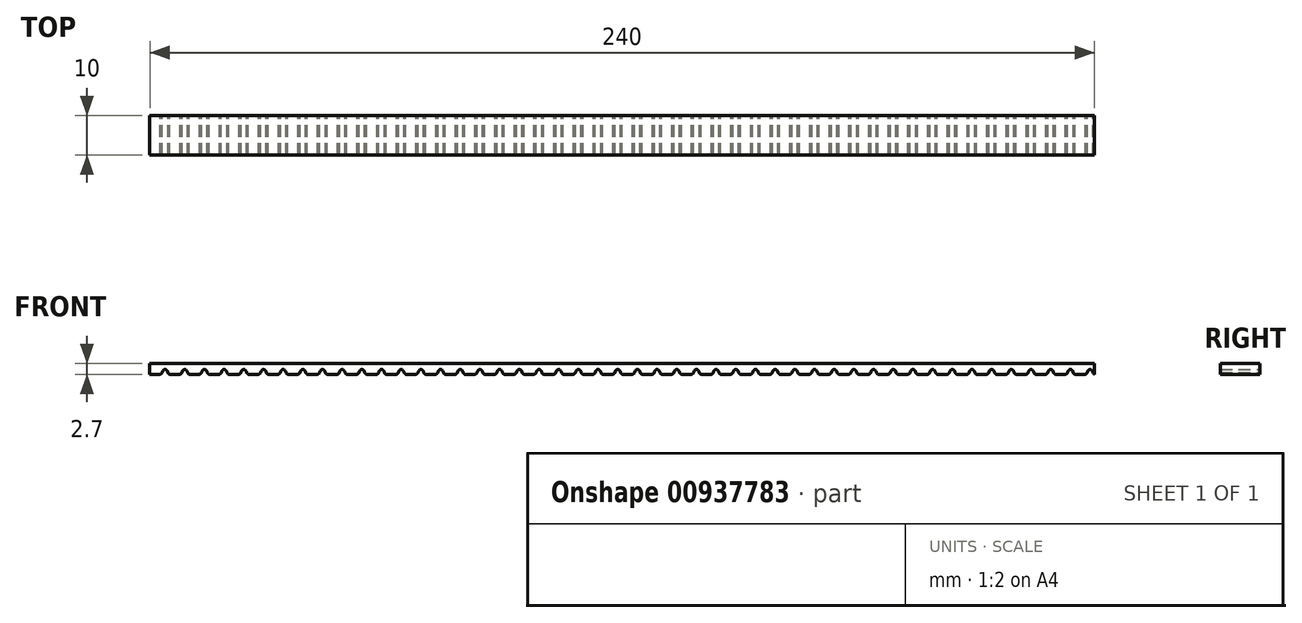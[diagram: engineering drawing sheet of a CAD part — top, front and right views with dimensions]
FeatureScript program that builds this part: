
annotation { "Feature Type Name" : "Feature", "Feature Type Description" : "" }
export const myFeature = defineFeature(function(context is Context, id is Id, definition is map)
    precondition{}
    {
        {
            var Q0;
            Q0=qCreatedBy(makeId("Front.planeOp"),FACE);
            var sketch = newSketch(context, id + "F0", { "sketchPlane" : qUnion([Q0])});
            skLineSegment(sketch, "E0", {"start": v(-120.76, -0.3) * mm, "end": v(-120.76, 0) * mm});
            skEllipticalArc(sketch, "E1.5.0.0", {});
            skArc(sketch, "E1.5.0.1", {"start": v(118.81, 0.14) * mm, "mid": v(118.98, -0.12) * mm, "end": v(119.24, -0.3) * mm});
            skArc(sketch, "E1.5.0.2", {"start": v(116.9, -0.3) * mm, "mid": v(117.2, -0.14) * mm, "end": v(117.39, 0.14) * mm});
            skEllipticalArc(sketch, "E1.5.0.3", {});
            skArc(sketch, "E2.1.0.0", {"start": v(113.81, 0.14) * mm, "mid": v(113.98, -0.12) * mm, "end": v(114.24, -0.3) * mm});
            skEllipticalArc(sketch, "E2.1.0.1", {});
            skEllipticalArc(sketch, "E2.1.0.2", {});
            skArc(sketch, "E2.1.0.3", {"start": v(111.9, -0.3) * mm, "mid": v(112.2, -0.14) * mm, "end": v(112.39, 0.14) * mm});
            skArc(sketch, "E2.2.0.0", {"start": v(108.81, 0.14) * mm, "mid": v(108.98, -0.12) * mm, "end": v(109.24, -0.3) * mm});
            skEllipticalArc(sketch, "E2.2.0.1", {});
            skEllipticalArc(sketch, "E2.2.0.2", {});
            skArc(sketch, "E2.2.0.3", {"start": v(106.9, -0.3) * mm, "mid": v(107.2, -0.14) * mm, "end": v(107.39, 0.14) * mm});
            skArc(sketch, "E2.3.0.0", {"start": v(103.81, 0.14) * mm, "mid": v(103.98, -0.12) * mm, "end": v(104.24, -0.3) * mm});
            skEllipticalArc(sketch, "E2.3.0.1", {});
            skEllipticalArc(sketch, "E2.3.0.2", {});
            skArc(sketch, "E2.3.0.3", {"start": v(101.9, -0.3) * mm, "mid": v(102.2, -0.14) * mm, "end": v(102.39, 0.14) * mm});
            skArc(sketch, "E2.4.0.0", {"start": v(98.81, 0.14) * mm, "mid": v(98.98, -0.12) * mm, "end": v(99.24, -0.3) * mm});
            skEllipticalArc(sketch, "E2.4.0.1", {});
            skEllipticalArc(sketch, "E2.4.0.2", {});
            skArc(sketch, "E2.4.0.3", {"start": v(96.9, -0.3) * mm, "mid": v(97.2, -0.14) * mm, "end": v(97.39, 0.14) * mm});
            skArc(sketch, "E2.5.0.0", {"start": v(93.81, 0.14) * mm, "mid": v(93.98, -0.12) * mm, "end": v(94.24, -0.3) * mm});
            skEllipticalArc(sketch, "E2.5.0.1", {});
            skEllipticalArc(sketch, "E2.5.0.2", {});
            skArc(sketch, "E2.5.0.3", {"start": v(91.9, -0.3) * mm, "mid": v(92.2, -0.14) * mm, "end": v(92.39, 0.14) * mm});
            skArc(sketch, "E2.6.0.0", {"start": v(88.81, 0.14) * mm, "mid": v(88.98, -0.12) * mm, "end": v(89.24, -0.3) * mm});
            skEllipticalArc(sketch, "E2.6.0.1", {});
            skEllipticalArc(sketch, "E2.6.0.2", {});
            skArc(sketch, "E2.6.0.3", {"start": v(86.9, -0.3) * mm, "mid": v(87.2, -0.14) * mm, "end": v(87.39, 0.14) * mm});
            skArc(sketch, "E2.7.0.0", {"start": v(83.81, 0.14) * mm, "mid": v(83.98, -0.12) * mm, "end": v(84.24, -0.3) * mm});
            skEllipticalArc(sketch, "E2.7.0.1", {});
            skEllipticalArc(sketch, "E2.7.0.2", {});
            skArc(sketch, "E2.7.0.3", {"start": v(81.9, -0.3) * mm, "mid": v(82.2, -0.14) * mm, "end": v(82.39, 0.14) * mm});
            skArc(sketch, "E2.8.0.0", {"start": v(78.81, 0.14) * mm, "mid": v(78.98, -0.12) * mm, "end": v(79.24, -0.3) * mm});
            skEllipticalArc(sketch, "E2.8.0.1", {});
            skEllipticalArc(sketch, "E2.8.0.2", {});
            skArc(sketch, "E2.8.0.3", {"start": v(76.9, -0.3) * mm, "mid": v(77.2, -0.14) * mm, "end": v(77.39, 0.14) * mm});
            skArc(sketch, "E2.9.0.0", {"start": v(73.81, 0.14) * mm, "mid": v(73.98, -0.12) * mm, "end": v(74.24, -0.3) * mm});
            skEllipticalArc(sketch, "E2.9.0.1", {});
            skEllipticalArc(sketch, "E2.9.0.2", {});
            skArc(sketch, "E2.9.0.3", {"start": v(71.9, -0.3) * mm, "mid": v(72.2, -0.14) * mm, "end": v(72.39, 0.14) * mm});
            skArc(sketch, "E2.10.0.0", {"start": v(68.81, 0.14) * mm, "mid": v(68.98, -0.12) * mm, "end": v(69.24, -0.3) * mm});
            skEllipticalArc(sketch, "E2.10.0.1", {});
            skEllipticalArc(sketch, "E2.10.0.2", {});
            skArc(sketch, "E2.10.0.3", {"start": v(66.9, -0.3) * mm, "mid": v(67.2, -0.14) * mm, "end": v(67.39, 0.14) * mm});
            skArc(sketch, "E2.11.0.0", {"start": v(63.81, 0.14) * mm, "mid": v(63.98, -0.12) * mm, "end": v(64.24, -0.3) * mm});
            skEllipticalArc(sketch, "E2.11.0.1", {});
            skEllipticalArc(sketch, "E2.11.0.2", {});
            skArc(sketch, "E2.11.0.3", {"start": v(61.9, -0.3) * mm, "mid": v(62.2, -0.14) * mm, "end": v(62.39, 0.14) * mm});
            skArc(sketch, "E2.12.0.0", {"start": v(58.81, 0.14) * mm, "mid": v(58.98, -0.12) * mm, "end": v(59.24, -0.3) * mm});
            skEllipticalArc(sketch, "E2.12.0.1", {});
            skEllipticalArc(sketch, "E2.12.0.2", {});
            skArc(sketch, "E2.12.0.3", {"start": v(56.9, -0.3) * mm, "mid": v(57.2, -0.14) * mm, "end": v(57.39, 0.14) * mm});
            skArc(sketch, "E2.13.0.0", {"start": v(53.81, 0.14) * mm, "mid": v(53.98, -0.12) * mm, "end": v(54.24, -0.3) * mm});
            skEllipticalArc(sketch, "E2.13.0.1", {});
            skEllipticalArc(sketch, "E2.13.0.2", {});
            skArc(sketch, "E2.13.0.3", {"start": v(51.9, -0.3) * mm, "mid": v(52.2, -0.14) * mm, "end": v(52.39, 0.14) * mm});
            skArc(sketch, "E2.14.0.0", {"start": v(48.81, 0.14) * mm, "mid": v(48.98, -0.12) * mm, "end": v(49.24, -0.3) * mm});
            skEllipticalArc(sketch, "E2.14.0.1", {});
            skEllipticalArc(sketch, "E2.14.0.2", {});
            skArc(sketch, "E2.14.0.3", {"start": v(46.9, -0.3) * mm, "mid": v(47.2, -0.14) * mm, "end": v(47.39, 0.14) * mm});
            skArc(sketch, "E2.15.0.0", {"start": v(43.81, 0.14) * mm, "mid": v(43.98, -0.12) * mm, "end": v(44.24, -0.3) * mm});
            skEllipticalArc(sketch, "E2.15.0.1", {});
            skEllipticalArc(sketch, "E2.15.0.2", {});
            skArc(sketch, "E2.15.0.3", {"start": v(41.9, -0.3) * mm, "mid": v(42.2, -0.14) * mm, "end": v(42.39, 0.14) * mm});
            skArc(sketch, "E2.16.0.0", {"start": v(38.81, 0.14) * mm, "mid": v(38.98, -0.12) * mm, "end": v(39.24, -0.3) * mm});
            skEllipticalArc(sketch, "E2.16.0.1", {});
            skEllipticalArc(sketch, "E2.16.0.2", {});
            skArc(sketch, "E2.16.0.3", {"start": v(36.9, -0.3) * mm, "mid": v(37.2, -0.14) * mm, "end": v(37.39, 0.14) * mm});
            skArc(sketch, "E2.17.0.0", {"start": v(33.81, 0.14) * mm, "mid": v(33.98, -0.12) * mm, "end": v(34.24, -0.3) * mm});
            skEllipticalArc(sketch, "E2.17.0.1", {});
            skEllipticalArc(sketch, "E2.17.0.2", {});
            skArc(sketch, "E2.17.0.3", {"start": v(31.9, -0.3) * mm, "mid": v(32.2, -0.14) * mm, "end": v(32.39, 0.14) * mm});
            skArc(sketch, "E2.18.0.0", {"start": v(28.81, 0.14) * mm, "mid": v(28.98, -0.12) * mm, "end": v(29.24, -0.3) * mm});
            skEllipticalArc(sketch, "E2.18.0.1", {});
            skEllipticalArc(sketch, "E2.18.0.2", {});
            skArc(sketch, "E2.18.0.3", {"start": v(26.9, -0.3) * mm, "mid": v(27.2, -0.14) * mm, "end": v(27.39, 0.14) * mm});
            skArc(sketch, "E2.19.0.0", {"start": v(23.81, 0.14) * mm, "mid": v(23.98, -0.12) * mm, "end": v(24.24, -0.3) * mm});
            skEllipticalArc(sketch, "E2.19.0.1", {});
            skEllipticalArc(sketch, "E2.19.0.2", {});
            skArc(sketch, "E2.19.0.3", {"start": v(21.9, -0.3) * mm, "mid": v(22.2, -0.14) * mm, "end": v(22.39, 0.14) * mm});
            skArc(sketch, "E2.20.0.0", {"start": v(18.81, 0.14) * mm, "mid": v(18.98, -0.12) * mm, "end": v(19.24, -0.3) * mm});
            skEllipticalArc(sketch, "E2.20.0.1", {});
            skEllipticalArc(sketch, "E2.20.0.2", {});
            skArc(sketch, "E2.20.0.3", {"start": v(16.9, -0.3) * mm, "mid": v(17.2, -0.14) * mm, "end": v(17.39, 0.14) * mm});
            skArc(sketch, "E2.21.0.0", {"start": v(13.81, 0.14) * mm, "mid": v(13.98, -0.12) * mm, "end": v(14.24, -0.3) * mm});
            skEllipticalArc(sketch, "E2.21.0.1", {});
            skEllipticalArc(sketch, "E2.21.0.2", {});
            skArc(sketch, "E2.21.0.3", {"start": v(11.9, -0.3) * mm, "mid": v(12.2, -0.14) * mm, "end": v(12.39, 0.14) * mm});
            skArc(sketch, "E2.22.0.0", {"start": v(8.81, 0.14) * mm, "mid": v(8.98, -0.12) * mm, "end": v(9.24, -0.3) * mm});
            skEllipticalArc(sketch, "E2.22.0.1", {});
            skEllipticalArc(sketch, "E2.22.0.2", {});
            skArc(sketch, "E2.22.0.3", {"start": v(6.9, -0.3) * mm, "mid": v(7.2, -0.14) * mm, "end": v(7.39, 0.14) * mm});
            skArc(sketch, "E2.23.0.0", {"start": v(3.81, 0.14) * mm, "mid": v(3.98, -0.12) * mm, "end": v(4.24, -0.3) * mm});
            skEllipticalArc(sketch, "E2.23.0.1", {});
            skEllipticalArc(sketch, "E2.23.0.2", {});
            skArc(sketch, "E2.23.0.3", {"start": v(1.9, -0.3) * mm, "mid": v(2.2, -0.14) * mm, "end": v(2.39, 0.14) * mm});
            skArc(sketch, "E2.24.0.0", {"start": v(-1.19, 0.14) * mm, "mid": v(-1.02, -0.12) * mm, "end": v(-0.76, -0.3) * mm});
            skEllipticalArc(sketch, "E2.24.0.1", {});
            skEllipticalArc(sketch, "E2.24.0.2", {});
            skArc(sketch, "E2.24.0.3", {"start": v(-3.1, -0.3) * mm, "mid": v(-2.8, -0.14) * mm, "end": v(-2.61, 0.14) * mm});
            skArc(sketch, "E2.25.0.0", {"start": v(-6.19, 0.14) * mm, "mid": v(-6.02, -0.12) * mm, "end": v(-5.76, -0.3) * mm});
            skEllipticalArc(sketch, "E2.25.0.1", {});
            skEllipticalArc(sketch, "E2.25.0.2", {});
            skArc(sketch, "E2.25.0.3", {"start": v(-8.1, -0.3) * mm, "mid": v(-7.8, -0.14) * mm, "end": v(-7.61, 0.14) * mm});
            skArc(sketch, "E2.26.0.0", {"start": v(-11.19, 0.14) * mm, "mid": v(-11.02, -0.12) * mm, "end": v(-10.76, -0.3) * mm});
            skEllipticalArc(sketch, "E2.26.0.1", {});
            skEllipticalArc(sketch, "E2.26.0.2", {});
            skArc(sketch, "E2.26.0.3", {"start": v(-13.1, -0.3) * mm, "mid": v(-12.8, -0.14) * mm, "end": v(-12.61, 0.14) * mm});
            skArc(sketch, "E2.27.0.0", {"start": v(-16.19, 0.14) * mm, "mid": v(-16.02, -0.12) * mm, "end": v(-15.76, -0.3) * mm});
            skEllipticalArc(sketch, "E2.27.0.1", {});
            skEllipticalArc(sketch, "E2.27.0.2", {});
            skArc(sketch, "E2.27.0.3", {"start": v(-18.1, -0.3) * mm, "mid": v(-17.8, -0.14) * mm, "end": v(-17.61, 0.14) * mm});
            skArc(sketch, "E2.28.0.0", {"start": v(-21.19, 0.14) * mm, "mid": v(-21.02, -0.12) * mm, "end": v(-20.76, -0.3) * mm});
            skEllipticalArc(sketch, "E2.28.0.1", {});
            skEllipticalArc(sketch, "E2.28.0.2", {});
            skArc(sketch, "E2.28.0.3", {"start": v(-23.1, -0.3) * mm, "mid": v(-22.8, -0.14) * mm, "end": v(-22.61, 0.14) * mm});
            skArc(sketch, "E2.29.0.0", {"start": v(-26.19, 0.14) * mm, "mid": v(-26.02, -0.12) * mm, "end": v(-25.76, -0.3) * mm});
            skEllipticalArc(sketch, "E2.29.0.1", {});
            skEllipticalArc(sketch, "E2.29.0.2", {});
            skArc(sketch, "E2.29.0.3", {"start": v(-28.1, -0.3) * mm, "mid": v(-27.8, -0.14) * mm, "end": v(-27.61, 0.14) * mm});
            skArc(sketch, "E2.30.0.0", {"start": v(-31.19, 0.14) * mm, "mid": v(-31.02, -0.12) * mm, "end": v(-30.76, -0.3) * mm});
            skEllipticalArc(sketch, "E2.30.0.1", {});
            skEllipticalArc(sketch, "E2.30.0.2", {});
            skArc(sketch, "E2.30.0.3", {"start": v(-33.1, -0.3) * mm, "mid": v(-32.8, -0.14) * mm, "end": v(-32.61, 0.14) * mm});
            skArc(sketch, "E2.31.0.0", {"start": v(-36.19, 0.14) * mm, "mid": v(-36.02, -0.12) * mm, "end": v(-35.76, -0.3) * mm});
            skEllipticalArc(sketch, "E2.31.0.1", {});
            skEllipticalArc(sketch, "E2.31.0.2", {});
            skArc(sketch, "E2.31.0.3", {"start": v(-38.1, -0.3) * mm, "mid": v(-37.8, -0.14) * mm, "end": v(-37.61, 0.14) * mm});
            skArc(sketch, "E2.32.0.0", {"start": v(-41.19, 0.14) * mm, "mid": v(-41.02, -0.12) * mm, "end": v(-40.76, -0.3) * mm});
            skEllipticalArc(sketch, "E2.32.0.1", {});
            skEllipticalArc(sketch, "E2.32.0.2", {});
            skArc(sketch, "E2.32.0.3", {"start": v(-43.1, -0.3) * mm, "mid": v(-42.8, -0.14) * mm, "end": v(-42.61, 0.14) * mm});
            skArc(sketch, "E2.33.0.0", {"start": v(-46.19, 0.14) * mm, "mid": v(-46.02, -0.12) * mm, "end": v(-45.76, -0.3) * mm});
            skEllipticalArc(sketch, "E2.33.0.1", {});
            skEllipticalArc(sketch, "E2.33.0.2", {});
            skArc(sketch, "E2.33.0.3", {"start": v(-48.1, -0.3) * mm, "mid": v(-47.8, -0.14) * mm, "end": v(-47.61, 0.14) * mm});
            skArc(sketch, "E2.34.0.0", {"start": v(-51.19, 0.14) * mm, "mid": v(-51.02, -0.12) * mm, "end": v(-50.76, -0.3) * mm});
            skEllipticalArc(sketch, "E2.34.0.1", {});
            skEllipticalArc(sketch, "E2.34.0.2", {});
            skArc(sketch, "E2.34.0.3", {"start": v(-53.1, -0.3) * mm, "mid": v(-52.8, -0.14) * mm, "end": v(-52.61, 0.14) * mm});
            skArc(sketch, "E2.35.0.0", {"start": v(-56.19, 0.14) * mm, "mid": v(-56.02, -0.12) * mm, "end": v(-55.76, -0.3) * mm});
            skEllipticalArc(sketch, "E2.35.0.1", {});
            skEllipticalArc(sketch, "E2.35.0.2", {});
            skArc(sketch, "E2.35.0.3", {"start": v(-58.1, -0.3) * mm, "mid": v(-57.8, -0.14) * mm, "end": v(-57.61, 0.14) * mm});
            skArc(sketch, "E2.36.0.0", {"start": v(-61.19, 0.14) * mm, "mid": v(-61.02, -0.12) * mm, "end": v(-60.76, -0.3) * mm});
            skEllipticalArc(sketch, "E2.36.0.1", {});
            skEllipticalArc(sketch, "E2.36.0.2", {});
            skArc(sketch, "E2.36.0.3", {"start": v(-63.1, -0.3) * mm, "mid": v(-62.8, -0.14) * mm, "end": v(-62.61, 0.14) * mm});
            skArc(sketch, "E2.37.0.0", {"start": v(-66.19, 0.14) * mm, "mid": v(-66.02, -0.12) * mm, "end": v(-65.76, -0.3) * mm});
            skEllipticalArc(sketch, "E2.37.0.1", {});
            skEllipticalArc(sketch, "E2.37.0.2", {});
            skArc(sketch, "E2.37.0.3", {"start": v(-68.1, -0.3) * mm, "mid": v(-67.8, -0.14) * mm, "end": v(-67.61, 0.14) * mm});
            skArc(sketch, "E2.38.0.0", {"start": v(-71.19, 0.14) * mm, "mid": v(-71.02, -0.12) * mm, "end": v(-70.76, -0.3) * mm});
            skEllipticalArc(sketch, "E2.38.0.1", {});
            skEllipticalArc(sketch, "E2.38.0.2", {});
            skArc(sketch, "E2.38.0.3", {"start": v(-73.1, -0.3) * mm, "mid": v(-72.8, -0.14) * mm, "end": v(-72.61, 0.14) * mm});
            skArc(sketch, "E2.39.0.0", {"start": v(-76.19, 0.14) * mm, "mid": v(-76.02, -0.12) * mm, "end": v(-75.76, -0.3) * mm});
            skEllipticalArc(sketch, "E2.39.0.1", {});
            skEllipticalArc(sketch, "E2.39.0.2", {});
            skArc(sketch, "E2.39.0.3", {"start": v(-78.1, -0.3) * mm, "mid": v(-77.8, -0.14) * mm, "end": v(-77.61, 0.14) * mm});
            skArc(sketch, "E2.40.0.0", {"start": v(-81.19, 0.14) * mm, "mid": v(-81.02, -0.12) * mm, "end": v(-80.76, -0.3) * mm});
            skEllipticalArc(sketch, "E2.40.0.1", {});
            skEllipticalArc(sketch, "E2.40.0.2", {});
            skArc(sketch, "E2.40.0.3", {"start": v(-83.1, -0.3) * mm, "mid": v(-82.8, -0.14) * mm, "end": v(-82.61, 0.14) * mm});
            skArc(sketch, "E2.41.0.0", {"start": v(-86.19, 0.14) * mm, "mid": v(-86.02, -0.12) * mm, "end": v(-85.76, -0.3) * mm});
            skEllipticalArc(sketch, "E2.41.0.1", {});
            skEllipticalArc(sketch, "E2.41.0.2", {});
            skArc(sketch, "E2.41.0.3", {"start": v(-88.1, -0.3) * mm, "mid": v(-87.8, -0.14) * mm, "end": v(-87.61, 0.14) * mm});
            skArc(sketch, "E2.42.0.0", {"start": v(-91.19, 0.14) * mm, "mid": v(-91.02, -0.12) * mm, "end": v(-90.76, -0.3) * mm});
            skEllipticalArc(sketch, "E2.42.0.1", {});
            skEllipticalArc(sketch, "E2.42.0.2", {});
            skArc(sketch, "E2.42.0.3", {"start": v(-93.1, -0.3) * mm, "mid": v(-92.8, -0.14) * mm, "end": v(-92.61, 0.14) * mm});
            skArc(sketch, "E2.43.0.0", {"start": v(-96.19, 0.14) * mm, "mid": v(-96.02, -0.12) * mm, "end": v(-95.76, -0.3) * mm});
            skEllipticalArc(sketch, "E2.43.0.1", {});
            skEllipticalArc(sketch, "E2.43.0.2", {});
            skArc(sketch, "E2.43.0.3", {"start": v(-98.1, -0.3) * mm, "mid": v(-97.8, -0.14) * mm, "end": v(-97.61, 0.14) * mm});
            skArc(sketch, "E2.44.0.0", {"start": v(-101.19, 0.14) * mm, "mid": v(-101.02, -0.12) * mm, "end": v(-100.76, -0.3) * mm});
            skEllipticalArc(sketch, "E2.44.0.1", {});
            skEllipticalArc(sketch, "E2.44.0.2", {});
            skArc(sketch, "E2.44.0.3", {"start": v(-103.1, -0.3) * mm, "mid": v(-102.8, -0.14) * mm, "end": v(-102.61, 0.14) * mm});
            skArc(sketch, "E2.45.0.0", {"start": v(-106.19, 0.14) * mm, "mid": v(-106.02, -0.12) * mm, "end": v(-105.76, -0.3) * mm});
            skEllipticalArc(sketch, "E2.45.0.1", {});
            skEllipticalArc(sketch, "E2.45.0.2", {});
            skArc(sketch, "E2.45.0.3", {"start": v(-108.1, -0.3) * mm, "mid": v(-107.8, -0.14) * mm, "end": v(-107.61, 0.14) * mm});
            skArc(sketch, "E2.46.0.0", {"start": v(-111.19, 0.14) * mm, "mid": v(-111.02, -0.12) * mm, "end": v(-110.76, -0.3) * mm});
            skEllipticalArc(sketch, "E2.46.0.1", {});
            skEllipticalArc(sketch, "E2.46.0.2", {});
            skArc(sketch, "E2.46.0.3", {"start": v(-113.1, -0.3) * mm, "mid": v(-112.8, -0.14) * mm, "end": v(-112.61, 0.14) * mm});
            skArc(sketch, "E2.47.0.0", {"start": v(-116.19, 0.14) * mm, "mid": v(-116.02, -0.12) * mm, "end": v(-115.76, -0.3) * mm});
            skEllipticalArc(sketch, "E2.47.0.1", {});
            skEllipticalArc(sketch, "E2.47.0.2", {});
            skArc(sketch, "E2.47.0.3", {"start": v(-118.1, -0.3) * mm, "mid": v(-117.8, -0.14) * mm, "end": v(-117.61, 0.14) * mm});
            skLineSegment(sketch, "E2.direction1", {"start": v(116.9, -0.3) * mm, "end": v(114.24, -0.3) * mm, "construction": true});
            skLineSegment(sketch, "E3.trimOffspring", {"start": v(-118.1, -0.3) * mm, "end": v(-120.76, -0.3) * mm});
            skLineSegment(sketch, "E4.trimOffspring", {"start": v(-113.1, -0.3) * mm, "end": v(-115.76, -0.3) * mm});
            skLineSegment(sketch, "E5", {"start": v(119.24, 0) * mm, "end": v(119.24, -0.3) * mm});
            skPoint(sketch, "E6.orphan", {"position": v(119.24, 0) * mm});
            skLineSegment(sketch, "E7.trimOffspring", {"start": v(111.9, -0.3) * mm, "end": v(109.24, -0.3) * mm});
            skLineSegment(sketch, "E8.trimOffspring", {"start": v(101.9, -0.3) * mm, "end": v(99.24, -0.3) * mm});
            skLineSegment(sketch, "E9.trimOffspring", {"start": v(106.9, -0.3) * mm, "end": v(104.24, -0.3) * mm});
            skLineSegment(sketch, "E10", {"start": v(116.9, -0.3) * mm, "end": v(114.24, -0.3) * mm});
            skLineSegment(sketch, "E11.trimOffspring", {"start": v(96.9, -0.3) * mm, "end": v(94.24, -0.3) * mm});
            skLineSegment(sketch, "E12.trimOffspring", {"start": v(91.9, -0.3) * mm, "end": v(89.24, -0.3) * mm});
            skLineSegment(sketch, "E13.trimOffspring", {"start": v(86.9, -0.3) * mm, "end": v(84.24, -0.3) * mm});
            skLineSegment(sketch, "E14.trimOffspring", {"start": v(81.9, -0.3) * mm, "end": v(79.24, -0.3) * mm});
            skLineSegment(sketch, "E15.trimOffspring", {"start": v(76.9, -0.3) * mm, "end": v(74.24, -0.3) * mm});
            skLineSegment(sketch, "E16.trimOffspring", {"start": v(71.9, -0.3) * mm, "end": v(69.24, -0.3) * mm});
            skLineSegment(sketch, "E17.trimOffspring", {"start": v(66.9, -0.3) * mm, "end": v(64.24, -0.3) * mm});
            skLineSegment(sketch, "E18.trimOffspring", {"start": v(61.9, -0.3) * mm, "end": v(59.24, -0.3) * mm});
            skLineSegment(sketch, "E19.trimOffspring", {"start": v(56.9, -0.3) * mm, "end": v(54.24, -0.3) * mm});
            skLineSegment(sketch, "E20.trimOffspring", {"start": v(51.9, -0.3) * mm, "end": v(49.24, -0.3) * mm});
            skLineSegment(sketch, "E21.trimOffspring", {"start": v(46.9, -0.3) * mm, "end": v(44.24, -0.3) * mm});
            skLineSegment(sketch, "E22.trimOffspring", {"start": v(41.9, -0.3) * mm, "end": v(39.24, -0.3) * mm});
            skLineSegment(sketch, "E23.trimOffspring", {"start": v(36.9, -0.3) * mm, "end": v(34.24, -0.3) * mm});
            skLineSegment(sketch, "E24.trimOffspring", {"start": v(31.9, -0.3) * mm, "end": v(29.24, -0.3) * mm});
            skLineSegment(sketch, "E25.trimOffspring", {"start": v(26.9, -0.3) * mm, "end": v(24.24, -0.3) * mm});
            skLineSegment(sketch, "E26.trimOffspring", {"start": v(21.9, -0.3) * mm, "end": v(19.24, -0.3) * mm});
            skLineSegment(sketch, "E27.trimOffspring", {"start": v(16.9, -0.3) * mm, "end": v(14.24, -0.3) * mm});
            skLineSegment(sketch, "E28.trimOffspring", {"start": v(11.9, -0.3) * mm, "end": v(9.24, -0.3) * mm});
            skLineSegment(sketch, "E29.trimOffspring", {"start": v(6.9, -0.3) * mm, "end": v(4.24, -0.3) * mm});
            skLineSegment(sketch, "E30.trimOffspring", {"start": v(1.9, -0.3) * mm, "end": v(-0.76, -0.3) * mm});
            skLineSegment(sketch, "E31.trimOffspring", {"start": v(-3.1, -0.3) * mm, "end": v(-5.76, -0.3) * mm});
            skLineSegment(sketch, "E32.trimOffspring", {"start": v(-8.1, -0.3) * mm, "end": v(-10.76, -0.3) * mm});
            skLineSegment(sketch, "E33.trimOffspring", {"start": v(-13.1, -0.3) * mm, "end": v(-15.76, -0.3) * mm});
            skLineSegment(sketch, "E34.trimOffspring", {"start": v(-18.1, -0.3) * mm, "end": v(-20.76, -0.3) * mm});
            skLineSegment(sketch, "E35.trimOffspring", {"start": v(-23.1, -0.3) * mm, "end": v(-25.76, -0.3) * mm});
            skLineSegment(sketch, "E36.trimOffspring", {"start": v(-28.1, -0.3) * mm, "end": v(-30.76, -0.3) * mm});
            skLineSegment(sketch, "E37.trimOffspring", {"start": v(-33.1, -0.3) * mm, "end": v(-35.76, -0.3) * mm});
            skLineSegment(sketch, "E38.trimOffspring", {"start": v(-38.1, -0.3) * mm, "end": v(-40.76, -0.3) * mm});
            skLineSegment(sketch, "E39.trimOffspring", {"start": v(-43.1, -0.3) * mm, "end": v(-45.76, -0.3) * mm});
            skLineSegment(sketch, "E40.trimOffspring", {"start": v(-48.1, -0.3) * mm, "end": v(-50.76, -0.3) * mm});
            skLineSegment(sketch, "E41.trimOffspring", {"start": v(-53.1, -0.3) * mm, "end": v(-55.76, -0.3) * mm});
            skLineSegment(sketch, "E42.trimOffspring", {"start": v(-58.1, -0.3) * mm, "end": v(-60.76, -0.3) * mm});
            skLineSegment(sketch, "E43.trimOffspring", {"start": v(-63.1, -0.3) * mm, "end": v(-65.76, -0.3) * mm});
            skLineSegment(sketch, "E44.trimOffspring", {"start": v(-68.1, -0.3) * mm, "end": v(-70.76, -0.3) * mm});
            skLineSegment(sketch, "E45.trimOffspring", {"start": v(-73.1, -0.3) * mm, "end": v(-75.76, -0.3) * mm});
            skLineSegment(sketch, "E46.trimOffspring", {"start": v(-78.1, -0.3) * mm, "end": v(-80.76, -0.3) * mm});
            skLineSegment(sketch, "E47.trimOffspring", {"start": v(-83.1, -0.3) * mm, "end": v(-85.76, -0.3) * mm});
            skLineSegment(sketch, "E48.trimOffspring", {"start": v(-88.1, -0.3) * mm, "end": v(-90.76, -0.3) * mm});
            skLineSegment(sketch, "E49.trimOffspring", {"start": v(-93.1, -0.3) * mm, "end": v(-95.76, -0.3) * mm});
            skLineSegment(sketch, "E50.trimOffspring", {"start": v(-98.1, -0.3) * mm, "end": v(-100.76, -0.3) * mm});
            skLineSegment(sketch, "E51.trimOffspring", {"start": v(-103.1, -0.3) * mm, "end": v(-105.76, -0.3) * mm});
            skLineSegment(sketch, "E52.trimOffspring", {"start": v(-108.1, -0.3) * mm, "end": v(-110.76, -0.3) * mm});
            skPoint(sketch, "E53.orphan", {"position": v(119.24, 2.4) * mm});
            skLineSegment(sketch, "E54", {"start": v(119.24, -0.3) * mm, "end": v(119.24, 2.4) * mm});
            skLineSegment(sketch, "E55", {"start": v(-120.76, -0.3) * mm, "end": v(-120.76, 2.4) * mm});
            skLineSegment(sketch, "E56", {"start": v(-120.76, 2.4) * mm, "end": v(119.24, 2.4) * mm});
            const initialGuessF0  = {"E1.5.0.0": [0.11808504036189091, -0.0001, 0, 1, 0.001, 0.0007199110732306023, 0, 1.3242255138486458], "E1.5.0.3": [0.11808504036189114, -0.0001, 0, 1, 0.001, 0.00075, 4.958959793090693, 0], "E2.1.0.1": [0.11308504036189114, -0.0001, 0, 1, 0.001, 0.00075, 4.958959793090693, 0], "E2.1.0.2": [0.1130850403618909, -0.0001, 0, 1, 0.001, 0.0007199110732306023, 0, 1.3242255138486458], "E2.2.0.1": [0.10808504036189115, -0.0001, 0, 1, 0.001, 0.00075, 4.958959793090693, 0], "E2.2.0.2": [0.10808504036189091, -0.0001, 0, 1, 0.001, 0.0007199110732306023, 0, 1.3242255138486458], "E2.3.0.1": [0.10308504036189114, -0.0001, 0, 1, 0.001, 0.00075, 4.958959793090693, 0], "E2.3.0.2": [0.10308504036189091, -0.0001, 0, 1, 0.001, 0.0007199110732306023, 0, 1.3242255138486458], "E2.4.0.1": [0.09808504036189114, -0.0001, 0, 1, 0.001, 0.00075, 4.958959793090693, 0], "E2.4.0.2": [0.0980850403618909, -0.0001, 0, 1, 0.001, 0.0007199110732306023, 0, 1.3242255138486458], "E2.5.0.1": [0.09308504036189114, -0.0001, 0, 1, 0.001, 0.00075, 4.95895979309069, 0], "E2.5.0.2": [0.09308504036189091, -0.0001, 0, 1, 0.001, 0.0007199110732306023, 0, 1.3242255138486458], "E2.6.0.1": [0.08808504036189115, -0.0001, 0, 1, 0.001, 0.00075, 4.958959793090693, 0], "E2.6.0.2": [0.08808504036189091, -0.0001, 0, 1, 0.001, 0.0007199110732306023, 0, 1.3242255138486458], "E2.7.0.1": [0.08308504036189114, -0.0001, 0, 1, 0.001, 0.00075, 4.958959793090693, 0], "E2.7.0.2": [0.0830850403618909, -0.0001, 0, 1, 0.001, 0.0007199110732306023, 0, 1.3242255138486458], "E2.8.0.1": [0.07808504036189115, -0.0001, 0, 1, 0.001, 0.00075, 4.9589597930906955, 0], "E2.8.0.2": [0.0780850403618909, -0.0001, 0, 1, 0.001, 0.0007199110732306023, 0, 1.3242255138486458], "E2.9.0.1": [0.07308504036189115, -0.0001, 0, 1, 0.001, 0.00075, 4.958959793090693, 0], "E2.9.0.2": [0.07308504036189091, -0.0001, 0, 1, 0.001, 0.0007199110732306023, 0, 1.3242255138486458], "E2.10.0.1": [0.06808504036189114, -0.0001, 0, 1, 0.001, 0.00075, 4.958959793090693, 0], "E2.10.0.2": [0.0680850403618909, -0.0001, 0, 1, 0.001, 0.0007199110732306023, 0, 1.3242255138486458], "E2.11.0.1": [0.06308504036189114, -0.0001, 0, 1, 0.001, 0.00075, 4.95895979309069, 0], "E2.11.0.2": [0.06308504036189092, -0.0001, 0, 1, 0.001, 0.0007199110732306023, 0, 1.324225513848647], "E2.12.0.1": [0.058085040361891146, -0.0001, 0, 1, 0.001, 0.00075, 4.958959793090693, 6.283185307179582], "E2.12.0.2": [0.05808504036189091, -0.0001, 0, 1, 0.001, 0.0007199110732306023, 0, 1.3242255138486458], "E2.13.0.1": [0.05308504036189114, -0.0001, 0, 1, 0.001, 0.00075, 4.958959793090693, 6.283185307179582], "E2.13.0.2": [0.053085040361890906, -0.0001, 0, 1, 0.001, 0.0007199110732306023, 0, 1.3242255138486458], "E2.14.0.1": [0.04808504036189114, -0.0001, 0, 1, 0.001, 0.00075, 4.958959793090693, 6.283185307179582], "E2.14.0.2": [0.0480850403618909, -0.0001, 0, 1, 0.001, 0.0007199110732306023, 0, 1.3242255138486458], "E2.15.0.1": [0.04308504036189115, -0.0001, 0, 1, 0.001, 0.00075, 4.958959793090693, 6.283185307179582], "E2.15.0.2": [0.04308504036189091, -0.0001, 0, 1, 0.001, 0.0007199110732306023, 0, 1.3242255138486458], "E2.16.0.1": [0.03808504036189114, -0.0001, 0, 1, 0.001, 0.00075, 4.958959793090693, 6.283185307179582], "E2.16.0.2": [0.03808504036189091, -0.0001, 0, 1, 0.001, 0.0007199110732306023, 0, 1.3242255138486458], "E2.17.0.1": [0.03308504036189114, -0.0001, 0, 1, 0.001, 0.00075, 4.958959793090693, 6.283185307179582], "E2.17.0.2": [0.0330850403618909, -0.0001, 0, 1, 0.001, 0.0007199110732306023, 0, 1.3242255138486458], "E2.18.0.1": [0.028085040361891148, -0.0001, 0, 1, 0.001, 0.00075, 4.958959793090693, 0], "E2.18.0.2": [0.02808504036189091, -0.0001, 0, 1, 0.001, 0.0007199110732306023, 0, 1.3242255138486458], "E2.19.0.1": [0.023085040361891143, -0.0001, 0, 1, 0.001, 0.00075, 4.958959793090693, 0], "E2.19.0.2": [0.023085040361890907, -0.0001, 0, 1, 0.001, 0.0007199110732306023, 0, 1.3242255138486458], "E2.20.0.1": [0.01808504036189114, -0.0001, 0, 1, 0.001, 0.00075, 4.958959793090693, 0], "E2.20.0.2": [0.018085040361890903, -0.0001, 0, 1, 0.001, 0.0007199110732306023, 0, 1.3242255138486458], "E2.21.0.1": [0.013085040361891148, -0.0001, 0, 1, 0.001, 0.00075, 4.958959793090693, 0], "E2.21.0.2": [0.013085040361890912, -0.0001, 0, 1, 0.001, 0.0007199110732306023, 0, 1.3242255138486458], "E2.22.0.1": [0.008085040361891144, -0.0001, 0, 1, 0.001, 0.00075, 4.958959793090693, 0], "E2.22.0.2": [0.008085040361890908, -0.0001, 0, 1, 0.001, 0.0007199110732306023, 0, 1.3242255138486458], "E2.23.0.1": [0.0030850403618911393, -0.0001, 0, 1, 0.001, 0.00075, 4.958959793090693, 0], "E2.23.0.2": [0.0030850403618909034, -0.0001, 0, 1, 0.001, 0.0007199110732306023, 0, 1.3242255138486458], "E2.24.0.1": [-0.0019149596381088513, -0.0001, 0, 1, 0.001, 0.00075, 4.958959793090693, 0], "E2.24.0.2": [-0.0019149596381090872, -0.0001, 0, 1, 0.001, 0.0007199110732306023, 0, 1.3242255138486458], "E2.25.0.1": [-0.006914959638108856, -0.0001, 0, 1, 0.001, 0.00075, 4.958959793090693, 0], "E2.25.0.2": [-0.006914959638109092, -0.0001, 0, 1, 0.001, 0.0007199110732306023, 0, 1.3242255138486458], "E2.26.0.1": [-0.01191495963810886, -0.0001, 0, 1, 0.001, 0.00075, 4.958959793090693, 0], "E2.26.0.2": [-0.011914959638109096, -0.0001, 0, 1, 0.001, 0.0007199110732306023, 0, 1.3242255138486458], "E2.27.0.1": [-0.016914959638108865, -0.0001, 0, 1, 0.001, 0.00075, 4.958959793090693, 0], "E2.27.0.2": [-0.0169149596381091, -0.0001, 0, 1, 0.001, 0.0007199110732306023, 0, 1.3242255138486458], "E2.28.0.1": [-0.02191495963810887, -0.0001, 0, 1, 0.001, 0.00075, 4.958959793090693, 0], "E2.28.0.2": [-0.021914959638109105, -0.0001, 0, 1, 0.001, 0.0007199110732306023, 0, 1.3242255138486458], "E2.29.0.1": [-0.026914959638108846, -0.0001, 0, 1, 0.001, 0.00075, 4.958959793090693, 0], "E2.29.0.2": [-0.02691495963810908, -0.0001, 0, 1, 0.001, 0.0007199110732306023, 0, 1.3242255138486458], "E2.30.0.1": [-0.03191495963810885, -0.0001, 0, 1, 0.001, 0.00075, 4.958959793090693, 6.283185307179582], "E2.30.0.2": [-0.031914959638109086, -0.0001, 0, 1, 0.001, 0.0007199110732306023, 0, 1.3242255138486458], "E2.31.0.1": [-0.036914959638108855, -0.0001, 0, 1, 0.001, 0.00075, 4.958959793090693, 6.283185307179582], "E2.31.0.2": [-0.03691495963810909, -0.0001, 0, 1, 0.001, 0.0007199110732306023, 0, 1.3242255138486458], "E2.32.0.1": [-0.04191495963810886, -0.0001, 0, 1, 0.001, 0.00075, 4.958959793090693, 6.283185307179582], "E2.32.0.2": [-0.041914959638109095, -0.0001, 0, 1, 0.001, 0.0007199110732306023, 0, 1.3242255138486458], "E2.33.0.1": [-0.046914959638108863, -0.0001, 0, 1, 0.001, 0.00075, 4.958959793090693, 6.283185307179582], "E2.33.0.2": [-0.0469149596381091, -0.0001, 0, 1, 0.001, 0.0007199110732306023, 0, 1.3242255138486458], "E2.34.0.1": [-0.05191495963810887, -0.0001, 0, 1, 0.001, 0.00075, 4.958959793090693, 6.283185307179582], "E2.34.0.2": [-0.051914959638109104, -0.0001, 0, 1, 0.001, 0.0007199110732306023, 0, 1.3242255138486458], "E2.35.0.1": [-0.05691495963810887, -0.0001, 0, 1, 0.001, 0.00075, 4.958959793090693, 6.283185307179582], "E2.35.0.2": [-0.05691495963810911, -0.0001, 0, 1, 0.001, 0.0007199110732306023, 0, 1.3242255138486458], "E2.36.0.1": [-0.06191495963810885, -0.0001, 0, 1, 0.001, 0.00075, 4.958959793090693, 6.283185307179582], "E2.36.0.2": [-0.061914959638109085, -0.0001, 0, 1, 0.001, 0.0007199110732306023, 0, 1.3242255138486458], "E2.37.0.1": [-0.06691495963810885, -0.0001, 0, 1, 0.001, 0.00075, 4.958959793090693, 0], "E2.37.0.2": [-0.06691495963810909, -0.0001, 0, 1, 0.001, 0.0007199110732306023, 0, 1.3242255138486458], "E2.38.0.1": [-0.07191495963810886, -0.0001, 0, 1, 0.001, 0.00075, 4.958959793090693, 0], "E2.38.0.2": [-0.0719149596381091, -0.0001, 0, 1, 0.001, 0.0007199110732306023, 0, 1.3242255138486458], "E2.39.0.1": [-0.07691495963810886, -0.0001, 0, 1, 0.001, 0.00075, 4.958959793090693, 0], "E2.39.0.2": [-0.0769149596381091, -0.0001, 0, 1, 0.001, 0.0007199110732306023, 0, 1.3242255138486458], "E2.40.0.1": [-0.08191495963810887, -0.0001, 0, 1, 0.001, 0.00075, 4.958959793090693, 0], "E2.40.0.2": [-0.0819149596381091, -0.0001, 0, 1, 0.001, 0.0007199110732306023, 0, 1.3242255138486458], "E2.41.0.1": [-0.08691495963810887, -0.0001, 0, 1, 0.001, 0.00075, 4.958959793090693, 0], "E2.41.0.2": [-0.08691495963810911, -0.0001, 0, 1, 0.001, 0.0007199110732306023, 0, 1.3242255138486458], "E2.42.0.1": [-0.09191495963810885, -0.0001, 0, 1, 0.001, 0.00075, 4.958959793090693, 0], "E2.42.0.2": [-0.09191495963810908, -0.0001, 0, 1, 0.001, 0.0007199110732306023, 0, 1.3242255138486458], "E2.43.0.1": [-0.09691495963810885, -0.0001, 0, 1, 0.001, 0.00075, 4.958959793090693, 0], "E2.43.0.2": [-0.09691495963810909, -0.0001, 0, 1, 0.001, 0.0007199110732306023, 0, 1.3242255138486458], "E2.44.0.1": [-0.10191495963810886, -0.0001, 0, 1, 0.001, 0.00075, 4.958959793090693, 0], "E2.44.0.2": [-0.10191495963810909, -0.0001, 0, 1, 0.001, 0.0007199110732306023, 0, 1.3242255138486458], "E2.45.0.1": [-0.10691495963810886, -0.0001, 0, 1, 0.001, 0.00075, 4.958959793090693, 0], "E2.45.0.2": [-0.1069149596381091, -0.0001, 0, 1, 0.001, 0.0007199110732306023, 0, 1.3242255138486458], "E2.46.0.1": [-0.11191495963810887, -0.0001, 0, 1, 0.001, 0.00075, 4.958959793090693, 0], "E2.46.0.2": [-0.1119149596381091, -0.0001, 0, 1, 0.001, 0.0007199110732306023, 0, 1.3242255138486458], "E2.47.0.1": [-0.11691495963810887, -0.0001, 0, 1, 0.001, 0.00075, 4.958959793090693, 0], "E2.47.0.2": [-0.1169149596381091, -0.0001, 0, 1, 0.001, 0.0007199110732306023, 0, 1.3242255138486458]};
            skSetInitialGuess(sketch, initialGuessF0);
            skSolve(sketch);
        }
        {
            var Q0;
            Q0=makeQuery(id+"F0.imprint","IMPRINT",FACE,{"disambiguationData":[TD([[makeQuery(id+"F0.imprint","IMPRINT",EDGE,{"derivedFrom":sQuery(id+"F0.wireOp",EDGE,"E1.5.0.0")}),-1.0]])]});
            extrude(context, id + "F1", {"entities" : qUnion([Q0]), "depth" : 10 * mm, "offsetDistance" : 25 * mm});
        }
    });
